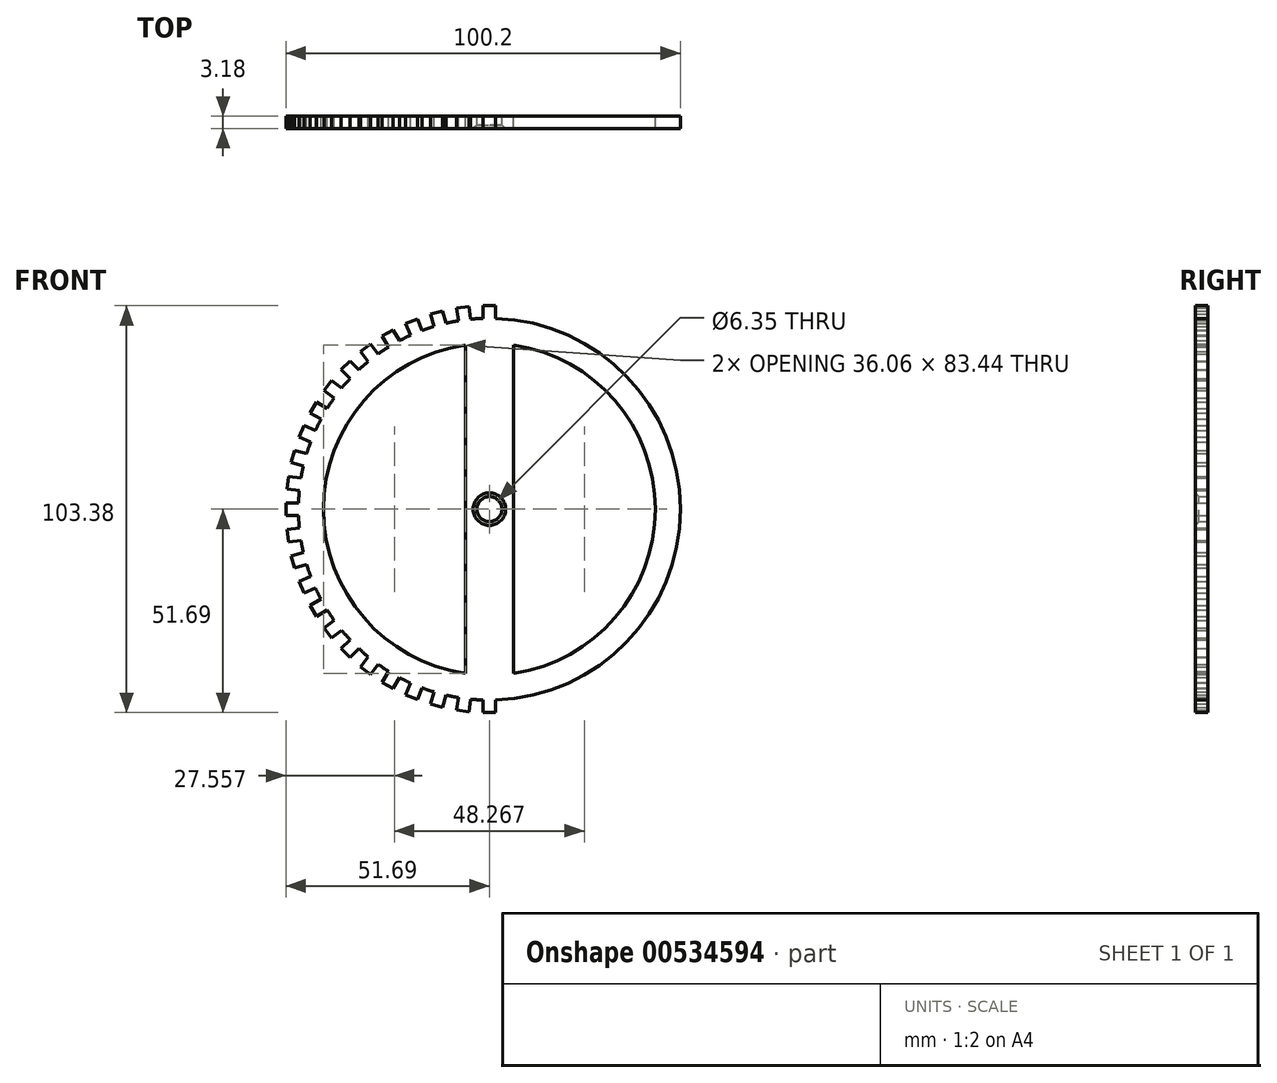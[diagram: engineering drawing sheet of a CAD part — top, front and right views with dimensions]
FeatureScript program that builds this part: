
annotation { "Feature Type Name" : "Feature", "Feature Type Description" : "" }
export const myFeature = defineFeature(function(context is Context, id is Id, definition is map)
    precondition{}
    {
        {
            var Q0;
            Q0=qCreatedBy(makeId("Front.planeOp"),FACE);
            var sketch = newSketch(context, id + "F0", { "sketchPlane" : qUnion([Q0])});
            skCircle(sketch, "E0", {"center": v(0, 0) * mm, "radius": 48.51 * mm});
            skCircle(sketch, "E1", {"center": v(0, 0) * mm, "radius": 42.16 * mm});
            skCircle(sketch, "E2", {"center": v(0, 0) * mm, "radius": 3.18 * mm});
            skLineSegment(sketch, "E3.bottom", {"start": v(6.1, 41.72) * mm, "end": v(-6.1, 41.72) * mm});
            skLineSegment(sketch, "E3.top", {"start": v(6.1, -41.72) * mm, "end": v(-6.1, -41.72) * mm});
            skLineSegment(sketch, "E3.left", {"start": v(6.1, 41.72) * mm, "end": v(6.1, -41.72) * mm});
            skLineSegment(sketch, "E3.right", {"start": v(-6.1, 41.72) * mm, "end": v(-6.1, -41.72) * mm});
            skPoint(sketch, "E4.middle", {"position": v(0, 48.51) * mm});
            skLineSegment(sketch, "E5.bottom", {"start": v(1.59, 51.69) * mm, "end": v(-1.59, 51.69) * mm});
            skLineSegment(sketch, "E5.top", {"start": v(1.59, 45.34) * mm, "end": v(-1.59, 45.34) * mm});
            skLineSegment(sketch, "E5.left", {"start": v(1.59, 51.69) * mm, "end": v(1.59, 45.34) * mm});
            skLineSegment(sketch, "E5.right", {"start": v(-1.59, 51.69) * mm, "end": v(-1.59, 45.34) * mm});
            skSolve(sketch);
        }
        {
            var Q0;
            {var subQ0=sQuery(id+"F0.wireOp",EDGE,"E3.bottom");Q0=makeQuery(id+"F0.imprint","IMPRINT",FACE,{"disambiguationData":[TD([[makeQuery(id+"F0.imprint","IMPRINT",EDGE,{"derivedFrom":subQ0}),-1.0]])]});}
            var Q1;
            {var subQ0=sQuery(id+"F0.wireOp",EDGE,"E3.top");Q1=makeQuery(id+"F0.imprint","IMPRINT",FACE,{"disambiguationData":[TD([[makeQuery(id+"F0.imprint","IMPRINT",EDGE,{"derivedFrom":subQ0}),1.0]])]});}
            var Q2;
            Q2=makeQuery(id+"F0.imprint","IMPRINT",FACE,{"disambiguationData":[TD([[makeQuery(id+"F0.imprint","IMPRINT",EDGE,{"derivedFrom":sQuery(id+"F0.wireOp",EDGE,"E2")}),-1.0]])]});
            var Q3;
            {var subQ9=sQuery(id+"F0.wireOp",EDGE,"E5.top");Q3=makeQuery(id+"F0.imprint","IMPRINT",FACE,{"disambiguationData":[TD([[makeQuery(id+"F0.imprint","IMPRINT",EDGE,{"derivedFrom":subQ9}),1.0]])]});}
            extrude(context, id + "F1", {"entities" : qUnion([Q0, Q1, Q2, Q3]), "endBound" : BoundingType.SYMMETRIC, "depth" : 3.17 * mm, "offsetDistance" : 25.4 * mm});
        }
        {
            var Q0;
            Q0=qCreatedBy(makeId("Right.planeOp"),FACE);
            var sketch = newSketch(context, id + "F2", { "sketchPlane" : qUnion([Q0])});
            skLineSegment(sketch, "E6", {"start": v(0, 0) * mm, "end": v(-49.79, 0) * mm});
            skSolve(sketch);
        }
        {
            var Q0;
            {var subQ5=sQuery(id+"F0.wireOp",EDGE,"E5.top");Q0=makeQuery(id+"F0.imprint","IMPRINT",FACE,{"disambiguationData":[TD([[makeQuery(id+"F0.imprint","IMPRINT",EDGE,{"derivedFrom":subQ5}),-1.0]])]});}
            extrude(context, id + "F3", {"entities" : qUnion([Q0]), "operationType" : NewBodyOperationType.ADD, "endBound" : BoundingType.SYMMETRIC, "depth" : 3.17 * mm, "offsetDistance" : 25.4 * mm});
        }
        {
            var Q0;
            {var subQ5=sQuery(id+"F0.wireOp",EDGE,"E5.bottom");Q0=makeQuery(id+"F0.imprint","IMPRINT",FACE,{"disambiguationData":[TD([[makeQuery(id+"F0.imprint","IMPRINT",EDGE,{"derivedFrom":subQ5}),1.0]])]});}
            extrude(context, id + "F4", {"entities" : qUnion([Q0]), "endBound" : BoundingType.SYMMETRIC, "depth" : 3.17 * mm, "offsetDistance" : 25.4 * mm});
        }
        {
            var Q0;
            Q0=makeQuery(id+"F4.opExtrude","SWEPT_BODY",BODY,{"disambiguationData":[OSD([sQuery(id+"F0.wireOp",EDGE,"E0"),sQuery(id+"F0.wireOp",EDGE,"E5.bottom"),sQuery(id+"F0.wireOp",EDGE,"E5.left"),sQuery(id+"F0.wireOp",EDGE,"E5.right")])]});
            var Q1;
            Q1=sQuery(id+"F2.wireOp",EDGE,"E6");
            circularPattern(context, id + "F5", {"operationType" : NewBodyOperationType.ADD, "entities" : qUnion([Q0]), "axis" : qUnion([Q1]), "angle" : 180 * degree, "instanceCount" : 25, "equalSpace" : true});
        }
        {
            var Q0;
            {var subQ0=sQuery(id+"F0.wireOp",EDGE,"E5.right");var subQ1=sQuery(id+"F0.wireOp",EDGE,"E5.left");var subQ2=sQuery(id+"F0.wireOp",EDGE,"E0");var subQ3=makeQuery(id+"F4.opExtrude","CAP_FACE",FACE,{"disambiguationData":[OSD([subQ2,sQuery(id+"F0.wireOp",EDGE,"E5.bottom"),subQ1,subQ0])],"isStart":false});var subQ4=sQuery(id+"F0.wireOp",EDGE,"E5.top");Q0=makeQuery(id+"F5.boolean.opBoolean","MERGE",FACE,{"derivedFrom":[makeQuery(id+"F3.boolean.opBoolean","MERGE",FACE,{"derivedFrom":[makeQuery(id+"F1.opExtrude","CAP_FACE",FACE,{"disambiguationData":[OSD([subQ2,sQuery(id+"F0.wireOp",EDGE,"E1"),sQuery(id+"F0.wireOp",EDGE,"E2"),sQuery(id+"F0.wireOp",EDGE,"E3.left"),sQuery(id+"F0.wireOp",EDGE,"E3.right"),subQ4,subQ1,subQ0])],"isStart":false}),makeQuery(id+"F3.opExtrude","CAP_FACE",FACE,{"disambiguationData":[OSD([subQ2,subQ4,subQ1,subQ0])],"isStart":false})]}),subQ3,makeQuery(id+"F5.opPattern","COPY",FACE,{"derivedFrom":subQ3,"instanceName":"1"}),makeQuery(id+"F5.opPattern","COPY",FACE,{"derivedFrom":subQ3,"instanceName":"2"}),makeQuery(id+"F5.opPattern","COPY",FACE,{"derivedFrom":subQ3,"instanceName":"3"}),makeQuery(id+"F5.opPattern","COPY",FACE,{"derivedFrom":subQ3,"instanceName":"4"}),makeQuery(id+"F5.opPattern","COPY",FACE,{"derivedFrom":subQ3,"instanceName":"5"}),makeQuery(id+"F5.opPattern","COPY",FACE,{"derivedFrom":subQ3,"instanceName":"6"}),makeQuery(id+"F5.opPattern","COPY",FACE,{"derivedFrom":subQ3,"instanceName":"7"}),makeQuery(id+"F5.opPattern","COPY",FACE,{"derivedFrom":subQ3,"instanceName":"8"}),makeQuery(id+"F5.opPattern","COPY",FACE,{"derivedFrom":subQ3,"instanceName":"9"}),makeQuery(id+"F5.opPattern","COPY",FACE,{"derivedFrom":subQ3,"instanceName":"10"}),makeQuery(id+"F5.opPattern","COPY",FACE,{"derivedFrom":subQ3,"instanceName":"11"}),makeQuery(id+"F5.opPattern","COPY",FACE,{"derivedFrom":subQ3,"instanceName":"12"}),makeQuery(id+"F5.opPattern","COPY",FACE,{"derivedFrom":subQ3,"instanceName":"13"}),makeQuery(id+"F5.opPattern","COPY",FACE,{"derivedFrom":subQ3,"instanceName":"14"}),makeQuery(id+"F5.opPattern","COPY",FACE,{"derivedFrom":subQ3,"instanceName":"15"}),makeQuery(id+"F5.opPattern","COPY",FACE,{"derivedFrom":subQ3,"instanceName":"16"}),makeQuery(id+"F5.opPattern","COPY",FACE,{"derivedFrom":subQ3,"instanceName":"17"}),makeQuery(id+"F5.opPattern","COPY",FACE,{"derivedFrom":subQ3,"instanceName":"18"}),makeQuery(id+"F5.opPattern","COPY",FACE,{"derivedFrom":subQ3,"instanceName":"19"}),makeQuery(id+"F5.opPattern","COPY",FACE,{"derivedFrom":subQ3,"instanceName":"20"}),makeQuery(id+"F5.opPattern","COPY",FACE,{"derivedFrom":subQ3,"instanceName":"21"}),makeQuery(id+"F5.opPattern","COPY",FACE,{"derivedFrom":subQ3,"instanceName":"22"}),makeQuery(id+"F5.opPattern","COPY",FACE,{"derivedFrom":subQ3,"instanceName":"23"}),makeQuery(id+"F5.opPattern","COPY",FACE,{"derivedFrom":subQ3,"instanceName":"24"})]});}
            var sketch = newSketch(context, id + "F6", { "sketchPlane" : qUnion([Q0])});
            skCircle(sketch, "E7", {"center": v(0, 0) * mm, "radius": 4.13 * mm});
            skSolve(sketch);
        }
        {
            var Q0;
            Q0=makeQuery(id+"F6.imprint","IMPRINT",FACE,{"disambiguationData":[TD([[makeQuery(id+"F6.imprint","IMPRINT",EDGE,{"derivedFrom":sQuery(id+"F6.wireOp",EDGE,"E7")}),1.0]])]});
            var Q1;
            Q1=makeQuery(id+"F6.imprint","IMPRINT",FACE,{"disambiguationData":[TD([[makeQuery(id+"F6.imprint","IMPRINT",EDGE,{"derivedFrom":makeQuery(id+"F1.opExtrude","CAP_EDGE",EDGE,{"disambiguationData":[OSD([sQuery(id+"F0.wireOp",EDGE,"E2")])],"isStart":false})}),1.0]])]});
            extrude(context, id + "F7", {"entities" : qUnion([Q0, Q1]), "operationType" : NewBodyOperationType.REMOVE, "oppositeDirection" : true, "depth" : 2.54 * mm, "offsetDistance" : 25.4 * mm, "hasDraft" : true, "draftAngle" : 45 * degree, "draftPullDirection" : true});
        }
    });
